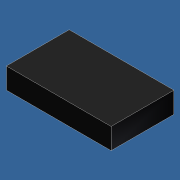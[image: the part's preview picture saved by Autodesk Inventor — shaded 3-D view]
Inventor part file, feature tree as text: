
AUTODESK INVENTOR PART (.ipt)
format: ipt  version: unknown  size: 166,400 bytes
history: native  units: mm
features: extrude x1, sketch x1
ambient origin geometry x8: Origin, YZ Plane, XZ Plane, XY Plane, X Axis, Y Axis, Z Axis, Center Point
feature tree (2):
  extrude  "Выдавливание2"  Depth=5.0mm
  sketch  "Эскиз2"
